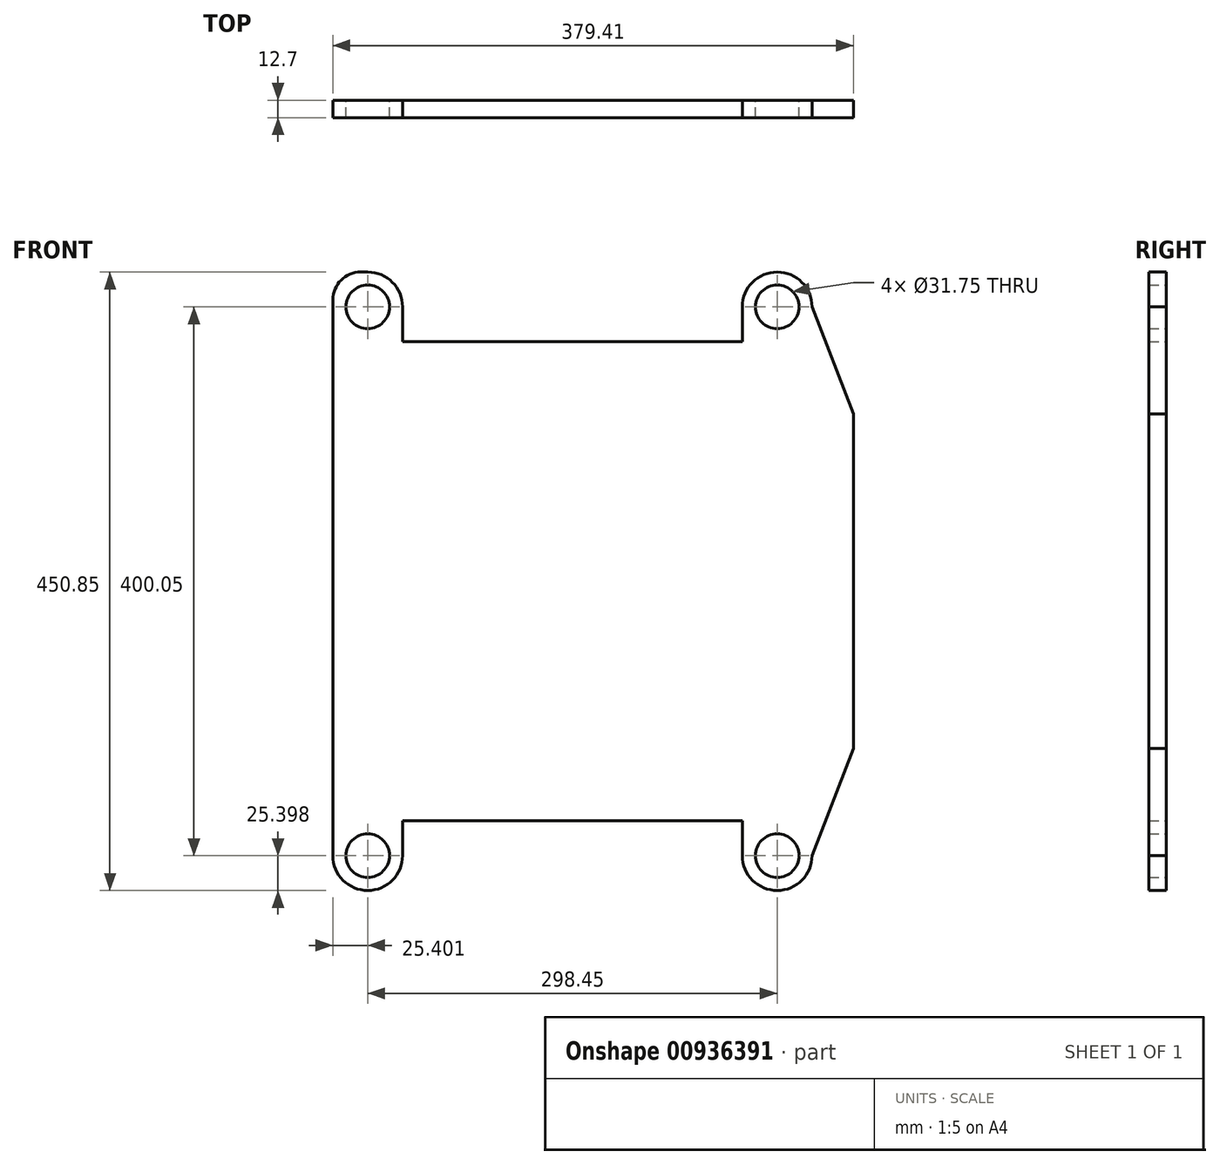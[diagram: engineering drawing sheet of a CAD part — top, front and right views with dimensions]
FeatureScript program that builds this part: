
annotation { "Feature Type Name" : "Feature", "Feature Type Description" : "" }
export const myFeature = defineFeature(function(context is Context, id is Id, definition is map)
    precondition{}
    {
        {
            var Q0;
            Q0=qCreatedBy(makeId("Front.planeOp"),FACE);
            var sketch = newSketch(context, id + "F0", { "sketchPlane" : qUnion([Q0])});
            skLineSegment(sketch, "E0.bottom", {"start": v(1.6, 451) * mm, "end": v(6.68, 451) * mm});
            skLineSegment(sketch, "E0.top", {"start": v(6.68, 0.16) * mm, "end": v(6.68, 0.16) * mm});
            skLineSegment(sketch, "E0.left", {"start": v(-18.72, 430.69) * mm, "end": v(-18.72, 25.56) * mm});
            skLineSegment(sketch, "E0.right", {"start": v(330.53, 425.6) * mm, "end": v(330.53, 25.56) * mm});
            skCircle(sketch, "E1", {"center": v(6.68, 425.6) * mm, "radius": 15.88 * mm});
            skCircle(sketch, "E2", {"center": v(305.13, 425.6) * mm, "radius": 15.88 * mm});
            skLineSegment(sketch, "E3", {"start": v(-18.72, 225.58) * mm, "end": v(330.53, 225.58) * mm, "construction": true});
            skCircle(sketch, "E4.MirrorC", {"center": v(6.68, 25.56) * mm, "radius": 15.88 * mm});
            skCircle(sketch, "E5.MirrorC", {"center": v(305.13, 25.56) * mm, "radius": 15.88 * mm});
            skPoint(sketch, "E6.visualSharp", {"position": v(-18.72, 451) * mm});
            skArc(sketch, "E6.filletArc", {"start": v(1.6, 451) * mm, "mid": v(-12.77, 445.06) * mm, "end": v(-18.72, 430.69) * mm});
            skPoint(sketch, "E7.visualSharp", {"position": v(330.53, 451) * mm});
            skArc(sketch, "E7.filletArc", {"start": v(330.53, 425.6) * mm, "mid": v(323.1, 443.57) * mm, "end": v(305.13, 451) * mm});
            skPoint(sketch, "E8.visualSharp", {"position": v(-18.72, 0.16) * mm});
            skArc(sketch, "E8.filletArc", {"start": v(-18.72, 25.56) * mm, "mid": v(-11.28, 7.6) * mm, "end": v(6.68, 0.16) * mm});
            skPoint(sketch, "E9.visualSharp", {"position": v(330.53, 0.16) * mm});
            skArc(sketch, "E9.filletArc", {"start": v(305.13, 0.16) * mm, "mid": v(323.1, 7.6) * mm, "end": v(330.53, 25.56) * mm});
            skLineSegment(sketch, "E10", {"start": v(32.08, 25.56) * mm, "end": v(32.08, 50.96) * mm});
            skLineSegment(sketch, "E11", {"start": v(32.08, 50.96) * mm, "end": v(279.73, 50.96) * mm});
            skLineSegment(sketch, "E12", {"start": v(279.73, 50.96) * mm, "end": v(279.73, 25.56) * mm});
            skLineSegment(sketch, "E13.trimOffspring", {"start": v(305.13, 0.16) * mm, "end": v(305.13, 0.16) * mm});
            skPoint(sketch, "E14.visualSharp", {"position": v(32.08, 0.16) * mm});
            skArc(sketch, "E14.filletArc", {"start": v(6.68, 0.16) * mm, "mid": v(24.64, 7.6) * mm, "end": v(32.08, 25.56) * mm});
            skPoint(sketch, "E15.newPointB", {"position": v(279.73, 0) * mm});
            skArc(sketch, "E15.filletArc", {"start": v(279.73, 25.56) * mm, "mid": v(287.17, 7.6) * mm, "end": v(305.13, 0.16) * mm});
            skLineSegment(sketch, "E16.MirrorCS", {"start": v(32.08, 400.2) * mm, "end": v(279.73, 400.2) * mm});
            skLineSegment(sketch, "E17.MirrorCS", {"start": v(32.08, 425.6) * mm, "end": v(32.08, 400.2) * mm});
            skArc(sketch, "E18.MirrorCS", {"start": v(6.68, 451) * mm, "mid": v(24.64, 443.57) * mm, "end": v(32.08, 425.6) * mm});
            skLineSegment(sketch, "E19.MirrorCS", {"start": v(279.73, 400.2) * mm, "end": v(279.73, 425.6) * mm});
            skArc(sketch, "E20.MirrorCS", {"start": v(279.73, 425.6) * mm, "mid": v(287.17, 443.57) * mm, "end": v(305.13, 451) * mm});
            skLineSegment(sketch, "E21", {"start": v(360.7, 347.45) * mm, "end": v(360.7, 103.71) * mm});
            skLineSegment(sketch, "E22", {"start": v(360.7, 347.45) * mm, "end": v(330.53, 425.6) * mm});
            skLineSegment(sketch, "E23.MirrorCS", {"start": v(360.7, 103.71) * mm, "end": v(330.53, 25.56) * mm});
            skPoint(sketch, "E24.orphan", {"position": v(360.7, 451) * mm});
            skPoint(sketch, "E25.orphan", {"position": v(360.7, 0) * mm});
            skLineSegment(sketch, "E26", {"start": v(305.13, 425.6) * mm, "end": v(305.13, 25.56) * mm, "construction": true});
            skSolve(sketch);
        }
        {
            var Q0;
            Q0=qSketchRegion(id+"F0",true);
            extrude(context, id + "F1", {"entities" : qUnion([Q0]), "depth" : 12.7 * mm, "offsetDistance" : 25.4 * mm});
        }
    });
